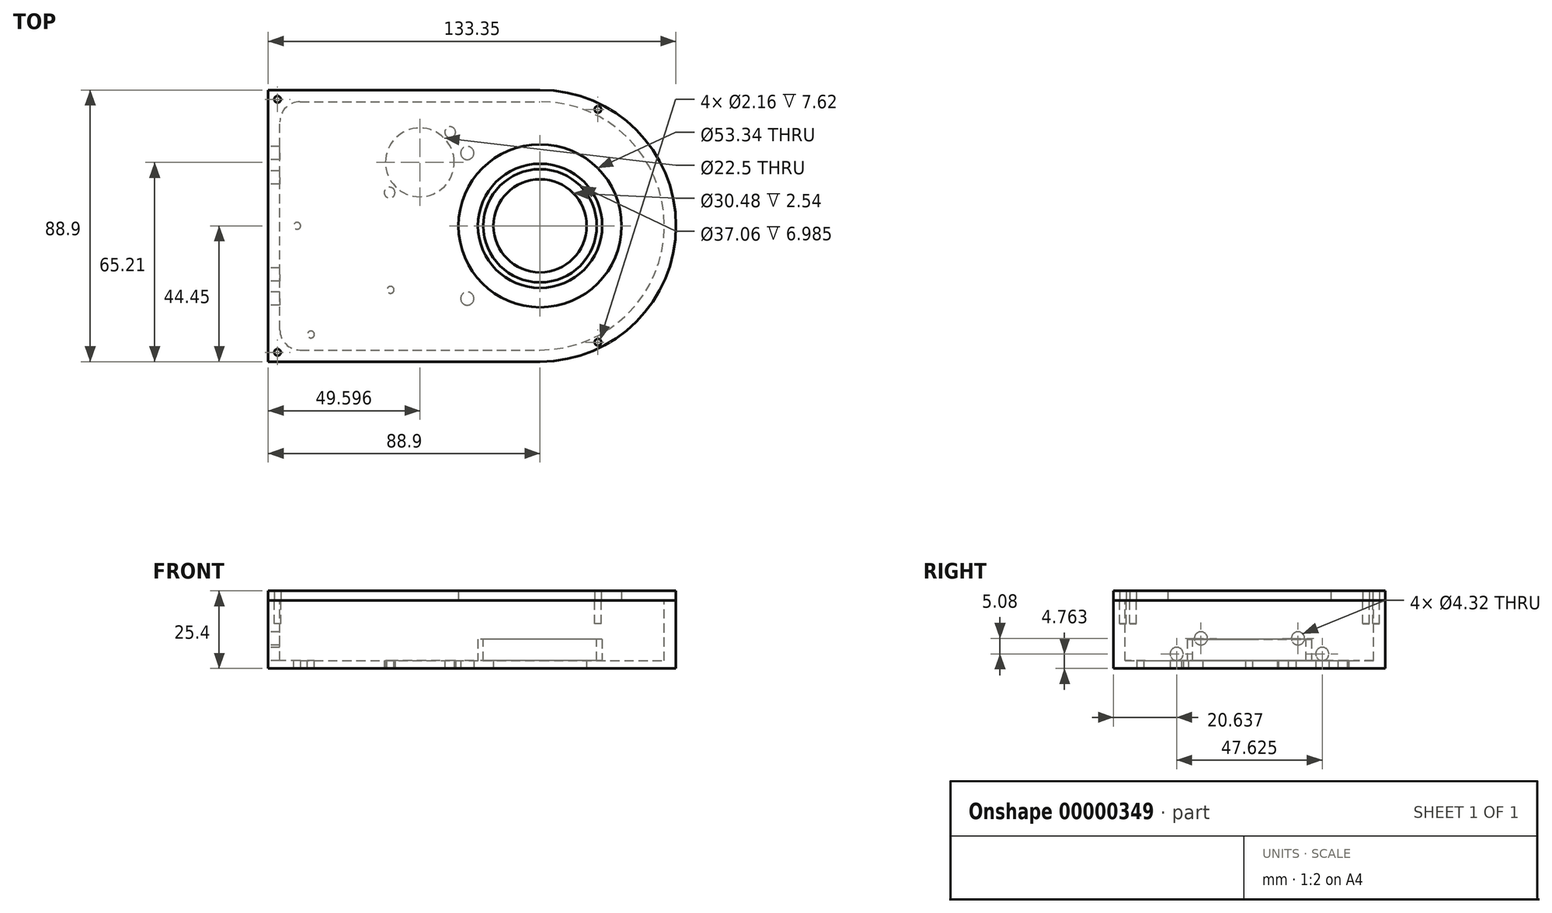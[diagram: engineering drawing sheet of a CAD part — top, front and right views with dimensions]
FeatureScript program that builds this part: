
annotation { "Feature Type Name" : "Feature", "Feature Type Description" : "" }
export const myFeature = defineFeature(function(context is Context, id is Id, definition is map)
    precondition{}
    {
        {
            var Q0;
            Q0=qCreatedBy(makeId("Top.planeOp"),FACE);
            var sketch = newSketch(context, id + "F0", { "sketchPlane" : qUnion([Q0])});
            skLineSegment(sketch, "E0.bottom", {"start": v(0, 0) * mm, "end": v(88.9, 0) * mm});
            skLineSegment(sketch, "E0.top", {"start": v(0, 88.9) * mm, "end": v(88.9, 88.9) * mm});
            skLineSegment(sketch, "E0.left", {"start": v(0, 0) * mm, "end": v(0, 88.9) * mm});
            skLineSegment(sketch, "E0.right", {"start": v(88.9, 0) * mm, "end": v(88.9, 88.9) * mm});
            skArc(sketch, "E1", {"start": v(88.9, 0) * mm, "mid": v(133.35, 44.45) * mm, "end": v(88.9, 88.9) * mm});
            skCircle(sketch, "E2", {"center": v(88.9, 44.45) * mm, "radius": 15.24 * mm});
            skCircle(sketch, "E3", {"center": v(88.9, 44.45) * mm, "radius": 31.75 * mm, "construction": true});
            skCircle(sketch, "E4", {"center": v(49.6, 65.21) * mm, "radius": 12.7 * mm, "construction": true});
            skCircle(sketch, "E5", {"center": v(49.6, 65.21) * mm, "radius": 11.25 * mm});
            skLineSegment(sketch, "E6.bottom", {"start": v(70.75, 86.36) * mm, "end": v(28.45, 86.36) * mm, "construction": true});
            skLineSegment(sketch, "E6.top", {"start": v(70.75, 44.06) * mm, "end": v(28.45, 44.06) * mm, "construction": true});
            skLineSegment(sketch, "E6.left", {"start": v(70.75, 86.36) * mm, "end": v(70.75, 44.06) * mm, "construction": true});
            skLineSegment(sketch, "E6.right", {"start": v(28.45, 86.36) * mm, "end": v(28.45, 44.06) * mm, "construction": true});
            skCircle(sketch, "E7", {"center": v(49.6, 65.21) * mm, "radius": 18 * mm, "construction": true});
            skCircle(sketch, "E8", {"center": v(88.9, 44.45) * mm, "radius": 22.23 * mm, "construction": true});
            skLineSegment(sketch, "E9", {"start": v(28.45, 44.06) * mm, "end": v(70.75, 86.36) * mm, "construction": true});
            skCircle(sketch, "E10", {"center": v(59.5, 75.1) * mm, "radius": 1.75 * mm});
            skCircle(sketch, "E11", {"center": v(39.7, 55.31) * mm, "radius": 1.75 * mm});
            skCircle(sketch, "E12", {"center": v(49.6, 65.21) * mm, "radius": 14 * mm, "construction": true});
            skSolve(sketch);
        }
        {
            var Q0;
            {var subQ4=sQuery(id+"F0.wireOp",EDGE,"E1");var subQ7=sQuery(id+"F0.wireOp",EDGE,"E0.bottom");Q0=qUnion([makeQuery(id+"F0.imprint","IMPRINT",FACE,{"disambiguationData":[TD([[makeQuery(id+"F0.imprint","IMPRINT",EDGE,{"derivedFrom":subQ7}),1.0]])]}),makeQuery(id+"F0.imprint","IMPRINT",FACE,{"disambiguationData":[TD([[makeQuery(id+"F0.imprint","IMPRINT",EDGE,{"derivedFrom":subQ4}),1.0]])]})]);}
            extrude(context, id + "F1", {"entities" : qUnion([Q0]), "depth" : 22.22 * mm});
        }
        {
            var Q0;
            Q0=makeQuery(id+"F1.opExtrude","CAP_FACE",FACE,{"disambiguationData":[OSD([sQuery(id+"F0.wireOp",EDGE,"E0.bottom"),sQuery(id+"F0.wireOp",EDGE,"E0.top"),sQuery(id+"F0.wireOp",EDGE,"E0.left"),sQuery(id+"F0.wireOp",EDGE,"E1"),sQuery(id+"F0.wireOp",EDGE,"E2")])],"isStart":false});
            var sketch = newSketch(context, id + "F2", { "sketchPlane" : qUnion([Q0])});
            skLineSegment(sketch, "E13.0", {"start": v(10.41, 85.1) * mm, "end": v(88.9, 85.1) * mm});
            skLineSegment(sketch, "E13.1", {"start": v(3.8, 10.41) * mm, "end": v(3.8, 78.49) * mm});
            skLineSegment(sketch, "E13.2", {"start": v(10.41, 3.8) * mm, "end": v(88.9, 3.8) * mm});
            skArc(sketch, "E13.3", {"start": v(88.9, 3.8) * mm, "mid": v(129.54, 44.45) * mm, "end": v(88.9, 85.1) * mm});
            skPoint(sketch, "E14.visualSharp", {"position": v(3.8, 85.1) * mm});
            skArc(sketch, "E14.filletArc", {"start": v(10.41, 85.1) * mm, "mid": v(5.74, 83.16) * mm, "end": v(3.8, 78.49) * mm});
            skPoint(sketch, "E15.visualSharp", {"position": v(3.8, 3.8) * mm});
            skArc(sketch, "E15.filletArc", {"start": v(3.8, 10.41) * mm, "mid": v(5.74, 5.74) * mm, "end": v(10.41, 3.8) * mm});
            skSolve(sketch);
        }
        {
            var Q0;
            {var subQ0=makeQuery(id+"F2.imprint","IMPRINT",EDGE,{"derivedFrom":makeQuery(id+"F1.opExtrude","CAP_EDGE",EDGE,{"disambiguationData":[OSD([sQuery(id+"F0.wireOp",EDGE,"E2")])],"isStart":false})});Q0=qUnion([makeQuery(id+"F2.imprint","IMPRINT",FACE,{"disambiguationData":[TD([[subQ0,1.0]])]}),makeQuery(id+"F2.imprint","IMPRINT",FACE,{"disambiguationData":[TD([[makeQuery(id+"F2.imprint","IMPRINT",EDGE,{"derivedFrom":sQuery(id+"F2.wireOp",EDGE,"E13.0")}),-1.0]])]})]);}
            extrude(context, id + "F3", {"entities" : qUnion([Q0]), "operationType" : NewBodyOperationType.REMOVE, "oppositeDirection" : true, "depth" : 19.68 * mm});
        }
        {
            var Q0;
            Q0=makeQuery(id+"F3.boolean.opBoolean","COPY",FACE,{"derivedFrom":makeQuery(id+"F3.opExtrude","CAP_FACE",FACE,{"disambiguationData":[OSD([sQuery(id+"F2.wireOp",EDGE,"E13.0"),sQuery(id+"F2.wireOp",EDGE,"E13.1"),sQuery(id+"F2.wireOp",EDGE,"E13.2"),sQuery(id+"F2.wireOp",EDGE,"E13.3"),sQuery(id+"F2.wireOp",EDGE,"E14.filletArc"),sQuery(id+"F2.wireOp",EDGE,"E15.filletArc")])],"isStart":false})});
            var sketch = newSketch(context, id + "F4", { "sketchPlane" : qUnion([Q0])});
            skArc(sketch, "E16.0", {"start": v(88.9, 3.8) * mm, "mid": v(129.54, 44.45) * mm, "end": v(88.9, 85.1) * mm, "construction": true});
            skCircle(sketch, "E17", {"center": v(88.9, 44.45) * mm, "radius": 20.32 * mm});
            skSolve(sketch);
        }
        {
            var Q0;
            {var subQ0=makeQuery(id+"F4.imprint","IMPRINT",EDGE,{"derivedFrom":makeQuery(id+"F3.boolean.opBoolean","INTERSECT",EDGE,{"derivedFrom":[makeQuery(id+"F1.opExtrude","SWEPT_FACE",FACE,{"disambiguationData":[OSD([sQuery(id+"F0.wireOp",EDGE,"E2")])]}),makeQuery(id+"F3.opExtrude","CAP_FACE",FACE,{"disambiguationData":[OSD([sQuery(id+"F2.wireOp",EDGE,"E13.0"),sQuery(id+"F2.wireOp",EDGE,"E13.1"),sQuery(id+"F2.wireOp",EDGE,"E13.2"),sQuery(id+"F2.wireOp",EDGE,"E13.3"),sQuery(id+"F2.wireOp",EDGE,"E14.filletArc"),sQuery(id+"F2.wireOp",EDGE,"E15.filletArc")])],"isStart":false})]})});Q0=qUnion([makeQuery(id+"F4.imprint","IMPRINT",FACE,{"disambiguationData":[TD([[subQ0,1.0]])]}),makeQuery(id+"F4.imprint","IMPRINT",FACE,{"disambiguationData":[TD([[makeQuery(id+"F4.imprint","IMPRINT",EDGE,{"derivedFrom":sQuery(id+"F4.wireOp",EDGE,"E17")}),1.0]])]})]);}
            extrude(context, id + "F5", {"entities" : qUnion([Q0]), "operationType" : NewBodyOperationType.ADD, "depth" : 7 * mm});
        }
        {
            var Q0;
            Q0=makeQuery(id+"F5.opExtrude","CAP_FACE",FACE,{"disambiguationData":[OSD([sQuery(id+"F4.wireOp",EDGE,"E17")])],"isStart":false});
            var sketch = newSketch(context, id + "F6", { "sketchPlane" : qUnion([Q0])});
            skCircle(sketch, "E18", {"center": v(88.9, 44.45) * mm, "radius": 18.53 * mm});
            skSolve(sketch);
        }
        {
            var Q0;
            Q0=makeQuery(id+"F6.imprint","IMPRINT",FACE,{"disambiguationData":[TD([[makeQuery(id+"F6.imprint","IMPRINT",EDGE,{"derivedFrom":sQuery(id+"F6.wireOp",EDGE,"E18")}),1.0]])]});
            extrude(context, id + "F7", {"entities" : qUnion([Q0]), "operationType" : NewBodyOperationType.REMOVE, "oppositeDirection" : true, "depth" : 7 * mm});
        }
        {
            var Q0;
            Q0=makeQuery(id+"F1.opExtrude","CAP_FACE",FACE,{"disambiguationData":[OSD([sQuery(id+"F0.wireOp",EDGE,"E0.bottom"),sQuery(id+"F0.wireOp",EDGE,"E0.top"),sQuery(id+"F0.wireOp",EDGE,"E0.left"),sQuery(id+"F0.wireOp",EDGE,"E1"),sQuery(id+"F0.wireOp",EDGE,"E2")])],"isStart":false});
            var sketch = newSketch(context, id + "F8", { "sketchPlane" : qUnion([Q0])});
            skLineSegment(sketch, "E19", {"start": v(3.05, 85.85) * mm, "end": v(107.83, 82.55) * mm, "construction": true});
            skLineSegment(sketch, "E20", {"start": v(107.83, 82.55) * mm, "end": v(107.83, 6.35) * mm, "construction": true});
            skLineSegment(sketch, "E21", {"start": v(107.83, 6.35) * mm, "end": v(3.05, 3.05) * mm, "construction": true});
            skCircle(sketch, "E22", {"center": v(3.05, 85.85) * mm, "radius": 1.08 * mm});
            skCircle(sketch, "E23", {"center": v(3.05, 3.05) * mm, "radius": 1.08 * mm});
            skCircle(sketch, "E24", {"center": v(107.83, 6.35) * mm, "radius": 1.08 * mm});
            skCircle(sketch, "E25", {"center": v(107.83, 82.55) * mm, "radius": 1.08 * mm});
            skSolve(sketch);
        }
        {
            var Q0;
            {Q0=qUnion([makeQuery(id+"F8.imprint","IMPRINT",FACE,{"disambiguationData":[TD([[makeQuery(id+"F8.imprint","IMPRINT",EDGE,{"derivedFrom":sQuery(id+"F8.wireOp",EDGE,"E22")}),1.0]])]}),makeQuery(id+"F8.imprint","IMPRINT",FACE,{"disambiguationData":[TD([[makeQuery(id+"F8.imprint","IMPRINT",EDGE,{"derivedFrom":sQuery(id+"F8.wireOp",EDGE,"E23")}),1.0]])]}),makeQuery(id+"F8.imprint","IMPRINT",FACE,{"disambiguationData":[TD([[makeQuery(id+"F8.imprint","IMPRINT",EDGE,{"derivedFrom":sQuery(id+"F8.wireOp",EDGE,"E24")}),1.0]])]}),makeQuery(id+"F8.imprint","IMPRINT",FACE,{"disambiguationData":[TD([[makeQuery(id+"F8.imprint","IMPRINT",EDGE,{"derivedFrom":sQuery(id+"F8.wireOp",EDGE,"E25")}),1.0]])]})]);}
            extrude(context, id + "F9", {"entities" : qUnion([Q0]), "operationType" : NewBodyOperationType.REMOVE, "oppositeDirection" : true, "depth" : 7.62 * mm});
        }
        {
            var Q0;
            Q0=makeQuery(id+"F1.opExtrude","CAP_FACE",FACE,{"disambiguationData":[OSD([sQuery(id+"F0.wireOp",EDGE,"E0.bottom"),sQuery(id+"F0.wireOp",EDGE,"E0.top"),sQuery(id+"F0.wireOp",EDGE,"E0.left"),sQuery(id+"F0.wireOp",EDGE,"E1"),sQuery(id+"F0.wireOp",EDGE,"E2")])],"isStart":false});
            var sketch = newSketch(context, id + "F10", { "sketchPlane" : qUnion([Q0])});
            skLineSegment(sketch, "E26.0", {"start": v(0, 88.9) * mm, "end": v(88.9, 88.9) * mm});
            skArc(sketch, "E27.0", {"start": v(88.9, 0) * mm, "mid": v(133.35, 44.45) * mm, "end": v(88.9, 88.9) * mm});
            skLineSegment(sketch, "E28.0", {"start": v(0, 0) * mm, "end": v(88.9, 0) * mm});
            skLineSegment(sketch, "E29.0", {"start": v(0, 0) * mm, "end": v(0, 88.9) * mm});
            skCircle(sketch, "E30", {"center": v(88.9, 44.45) * mm, "radius": 26.67 * mm});
            skCircle(sketch, "E31.0", {"center": v(3.05, 85.85) * mm, "radius": 1.08 * mm});
            skCircle(sketch, "E32.0", {"center": v(107.83, 82.55) * mm, "radius": 1.08 * mm});
            skCircle(sketch, "E33.0", {"center": v(107.83, 6.35) * mm, "radius": 1.08 * mm});
            skCircle(sketch, "E34.0", {"center": v(3.05, 3.05) * mm, "radius": 1.08 * mm});
            skSolve(sketch);
        }
        {
            var Q0;
            {Q0=qUnion([makeQuery(id+"F10.imprint","IMPRINT",FACE,{"disambiguationData":[TD([[makeQuery(id+"F10.imprint","IMPRINT",EDGE,{"derivedFrom":sQuery(id+"F10.wireOp",EDGE,"E30")}),-1.0]])]}),makeQuery(id+"F10.imprint","IMPRINT",FACE,{"disambiguationData":[TD([[makeQuery(id+"F10.imprint","IMPRINT",EDGE,{"derivedFrom":sQuery(id+"F10.wireOp",EDGE,"E26.0")}),-1.0]])]})]);}
            extrude(context, id + "F11", {"entities" : qUnion([Q0]), "depth" : 3.17 * mm});
        }
        {
            var Q0;
            Q0=makeQuery(id+"F1.opExtrude","SWEPT_FACE",FACE,{"disambiguationData":[OSD([sQuery(id+"F0.wireOp",EDGE,"E0.left")])]});
            var sketch = newSketch(context, id + "F12", { "sketchPlane" : qUnion([Q0])});
            skCircle(sketch, "E35", {"center": v(-68.26, 4.76) * mm, "radius": 2.16 * mm});
            skCircle(sketch, "E36", {"center": v(-20.64, 4.76) * mm, "radius": 2.16 * mm});
            skCircle(sketch, "E37", {"center": v(-60.33, 9.84) * mm, "radius": 2.16 * mm});
            skCircle(sketch, "E38", {"center": v(-28.58, 9.84) * mm, "radius": 2.16 * mm});
            skSolve(sketch);
        }
        {
            var Q0;
            {Q0=qUnion([makeQuery(id+"F12.imprint","IMPRINT",FACE,{"disambiguationData":[TD([[makeQuery(id+"F12.imprint","IMPRINT",EDGE,{"derivedFrom":sQuery(id+"F12.wireOp",EDGE,"E35")}),1.0]])]}),makeQuery(id+"F12.imprint","IMPRINT",FACE,{"disambiguationData":[TD([[makeQuery(id+"F12.imprint","IMPRINT",EDGE,{"derivedFrom":sQuery(id+"F12.wireOp",EDGE,"E36")}),1.0]])]}),makeQuery(id+"F12.imprint","IMPRINT",FACE,{"disambiguationData":[TD([[makeQuery(id+"F12.imprint","IMPRINT",EDGE,{"derivedFrom":sQuery(id+"F12.wireOp",EDGE,"E37")}),1.0]])]}),makeQuery(id+"F12.imprint","IMPRINT",FACE,{"disambiguationData":[TD([[makeQuery(id+"F12.imprint","IMPRINT",EDGE,{"derivedFrom":sQuery(id+"F12.wireOp",EDGE,"E38")}),1.0]])]})]);}
            var Q1;
            Q1=makeQuery(id+"F3.boolean.opBoolean","COPY",FACE,{"derivedFrom":makeQuery(id+"F3.opExtrude","SWEPT_FACE",FACE,{"disambiguationData":[OSD([sQuery(id+"F2.wireOp",EDGE,"E13.1")])]})});
            extrude(context, id + "F13", {"entities" : qUnion([Q0]), "operationType" : NewBodyOperationType.REMOVE, "endBound" : BoundingType.UP_TO_SURFACE, "oppositeDirection" : true, "endBoundEntityFace" : qUnion([Q1]), "depth" : 25.4 * mm});
        }
        {
            var Q0;
            Q0=makeQuery(id+"F1.opExtrude","CAP_FACE",FACE,{"disambiguationData":[OSD([sQuery(id+"F0.wireOp",EDGE,"E0.bottom"),sQuery(id+"F0.wireOp",EDGE,"E0.top"),sQuery(id+"F0.wireOp",EDGE,"E0.left"),sQuery(id+"F0.wireOp",EDGE,"E1"),sQuery(id+"F0.wireOp",EDGE,"E2")])],"isStart":true});
            var sketch = newSketch(context, id + "F14", { "sketchPlane" : qUnion([Q0])});
            skCircle(sketch, "E39", {"center": v(88.9, -44.45) * mm, "radius": 28.57 * mm, "construction": true});
            skLineSegment(sketch, "E40.bottom", {"start": v(60.32, -73.03) * mm, "end": v(117.47, -73.03) * mm, "construction": true});
            skLineSegment(sketch, "E40.top", {"start": v(60.32, -15.88) * mm, "end": v(117.47, -15.88) * mm, "construction": true});
            skLineSegment(sketch, "E40.left", {"start": v(60.32, -73.03) * mm, "end": v(60.32, -15.88) * mm, "construction": true});
            skLineSegment(sketch, "E40.right", {"start": v(117.47, -73.03) * mm, "end": v(117.47, -15.88) * mm, "construction": true});
            skCircle(sketch, "E41", {"center": v(65.09, -68.26) * mm, "radius": 2.16 * mm});
            skCircle(sketch, "E42", {"center": v(65.09, -20.64) * mm, "radius": 2.16 * mm});
            skSolve(sketch);
        }
        {
            var Q0;
            {Q0=qUnion([makeQuery(id+"F14.imprint","IMPRINT",FACE,{"disambiguationData":[TD([[makeQuery(id+"F14.imprint","IMPRINT",EDGE,{"derivedFrom":sQuery(id+"F14.wireOp",EDGE,"E41")}),1.0]])]}),makeQuery(id+"F14.imprint","IMPRINT",FACE,{"disambiguationData":[TD([[makeQuery(id+"F14.imprint","IMPRINT",EDGE,{"derivedFrom":sQuery(id+"F14.wireOp",EDGE,"E42")}),1.0]])]})]);}
            var Q1;
            Q1=makeQuery(id+"F11.opExtrude","CAP_FACE",FACE,{"disambiguationData":[OSD([sQuery(id+"F10.wireOp",EDGE,"E26.0"),sQuery(id+"F10.wireOp",EDGE,"E27.0"),sQuery(id+"F10.wireOp",EDGE,"E28.0"),sQuery(id+"F10.wireOp",EDGE,"E29.0"),sQuery(id+"F10.wireOp",EDGE,"E30"),sQuery(id+"F10.wireOp",EDGE,"E31.0"),sQuery(id+"F10.wireOp",EDGE,"E32.0"),sQuery(id+"F10.wireOp",EDGE,"E33.0"),sQuery(id+"F10.wireOp",EDGE,"E34.0")])],"isStart":true});
            extrude(context, id + "F15", {"entities" : qUnion([Q0]), "operationType" : NewBodyOperationType.REMOVE, "endBound" : BoundingType.UP_TO_BODY, "oppositeDirection" : true, "endBoundEntityBody" : qUnion([Q1]), "depth" : 25.4 * mm});
        }
        {
            var Q0;
            Q0=makeQuery(id+"F3.boolean.opBoolean","COPY",FACE,{"derivedFrom":makeQuery(id+"F3.opExtrude","CAP_FACE",FACE,{"disambiguationData":[OSD([sQuery(id+"F2.wireOp",EDGE,"E13.0"),sQuery(id+"F2.wireOp",EDGE,"E13.1"),sQuery(id+"F2.wireOp",EDGE,"E13.2"),sQuery(id+"F2.wireOp",EDGE,"E13.3"),sQuery(id+"F2.wireOp",EDGE,"E14.filletArc"),sQuery(id+"F2.wireOp",EDGE,"E15.filletArc")])],"isStart":false})});
            var sketch = newSketch(context, id + "F16", { "sketchPlane" : qUnion([Q0])});
            skCircle(sketch, "E43", {"center": v(9.46, 44.45) * mm, "radius": 1.13 * mm});
            skCircle(sketch, "E44", {"center": v(13.97, 8.88) * mm, "radius": 1.13 * mm});
            skCircle(sketch, "E45", {"center": v(40, 23.48) * mm, "radius": 1.13 * mm});
            skSolve(sketch);
        }
        {
            var Q0;
            Q0 = qSketchRegion(id + "F16", true);
            extrude(context, id + "F17", {"entities" : qUnion([Q0]), "operationType" : NewBodyOperationType.REMOVE, "endBound" : BoundingType.THROUGH_ALL, "oppositeDirection" : true, "depth" : 25.4 * mm});
        }
    });
